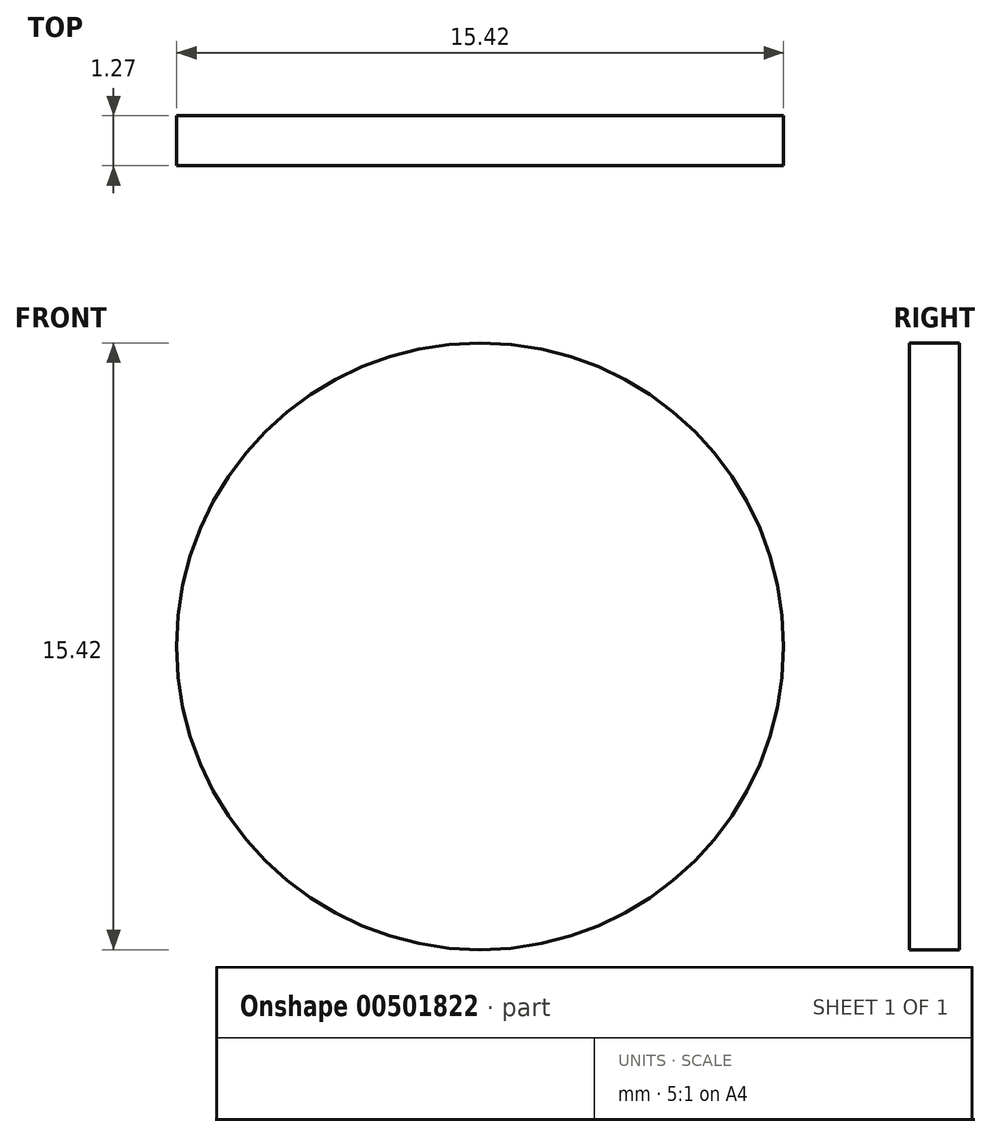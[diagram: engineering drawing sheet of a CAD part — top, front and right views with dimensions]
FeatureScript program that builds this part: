
annotation { "Feature Type Name" : "Feature", "Feature Type Description" : "" }
export const myFeature = defineFeature(function(context is Context, id is Id, definition is map)
    precondition{}
    {
        {
            var Q0;
            Q0=qCreatedBy(makeId("Front.planeOp"),FACE);
            var sketch = newSketch(context, id + "F0", { "sketchPlane" : qUnion([Q0])});
            skCircle(sketch, "E0", {"center": v(0, 0) * mm, "radius": 7.71 * mm});
            skSolve(sketch);
        }
        {
            var Q0;
            Q0=makeQuery(id+"F0.imprint","IMPRINT",FACE,{"disambiguationData":[TD([[makeQuery(id+"F0.imprint","IMPRINT",EDGE,{"derivedFrom":sQuery(id+"F0.wireOp",EDGE,"E0")}),1.0]])]});
            extrude(context, id + "F1", {"entities" : qUnion([Q0]), "depth" : 1.27 * mm});
        }
    });
